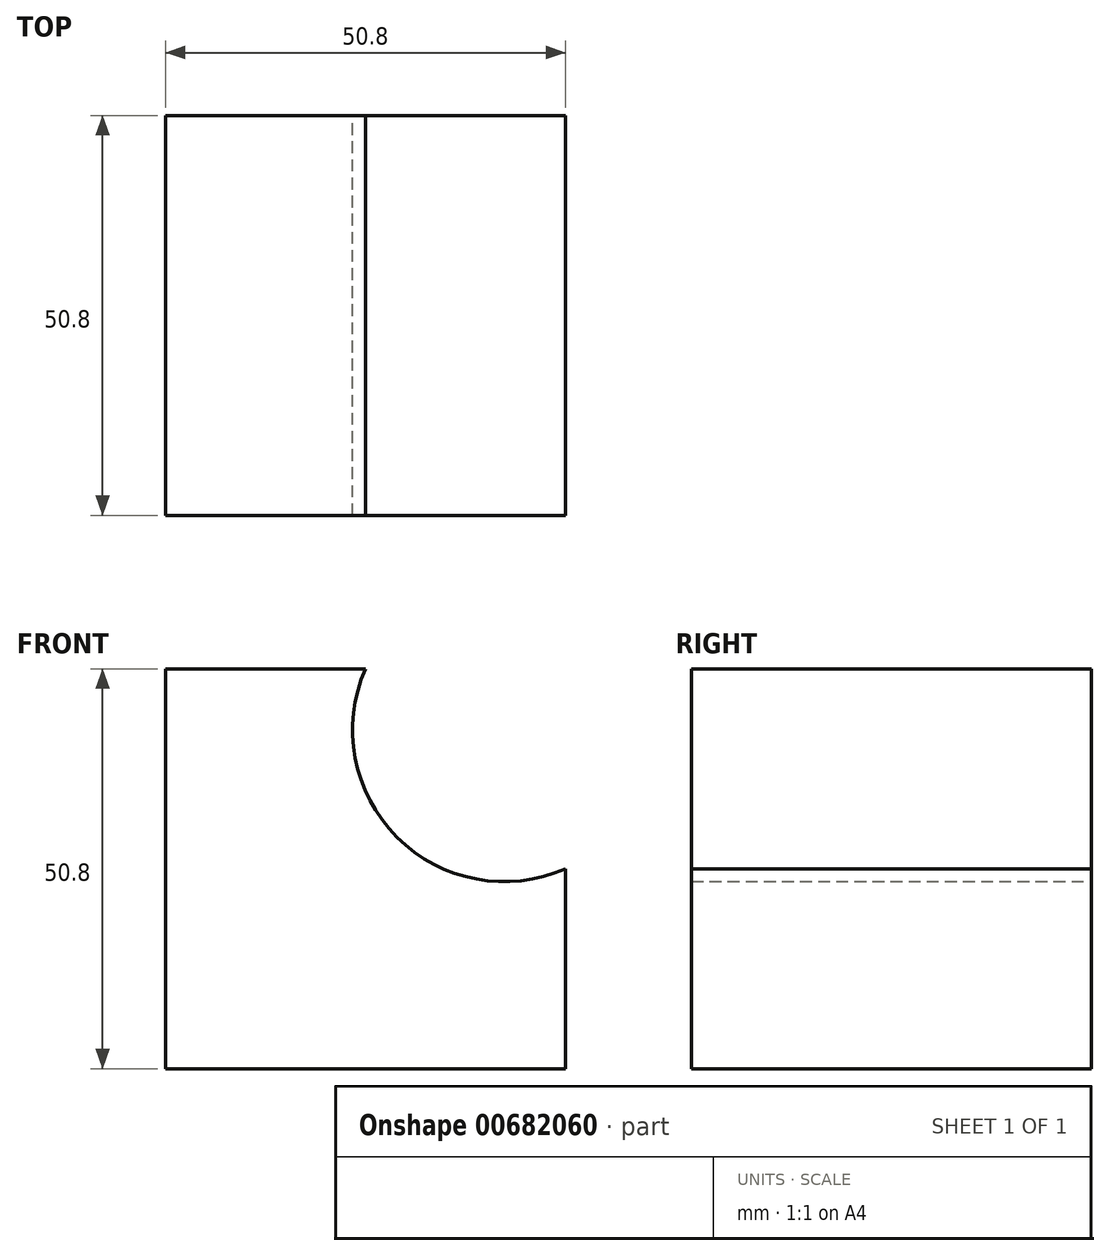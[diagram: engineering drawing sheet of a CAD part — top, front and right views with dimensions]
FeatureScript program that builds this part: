
annotation { "Feature Type Name" : "Feature", "Feature Type Description" : "" }
export const myFeature = defineFeature(function(context is Context, id is Id, definition is map)
    precondition{}
    {
        {
            var Q0;
            Q0=qCreatedBy(makeId("Front.planeOp"),FACE);
            var sketch = newSketch(context, id + "F0", { "sketchPlane" : qUnion([Q0])});
            skLineSegment(sketch, "E0", {"start": v(-50.8, 25.4) * mm, "end": v(-50.8, -25.4) * mm});
            skLineSegment(sketch, "E1", {"start": v(-50.8, -25.4) * mm, "end": v(0, -25.4) * mm});
            skLineSegment(sketch, "E2", {"start": v(-50.8, 25.4) * mm, "end": v(-25.4, 25.4) * mm});
            skLineSegment(sketch, "E3", {"start": v(0, -25.4) * mm, "end": v(0, 0) * mm});
            skArc(sketch, "E4", {"start": v(-25.4, 25.4) * mm, "mid": v(-21.4, 4) * mm, "end": v(0, 0) * mm});
            skSolve(sketch);
        }
        {
            var Q0;
            Q0 = qSketchRegion(id + "F0", true);
            extrude(context, id + "F1", {"entities" : qUnion([Q0]), "depth" : 50.8 * mm, "offsetDistance" : 25.4 * mm});
        }
    });
